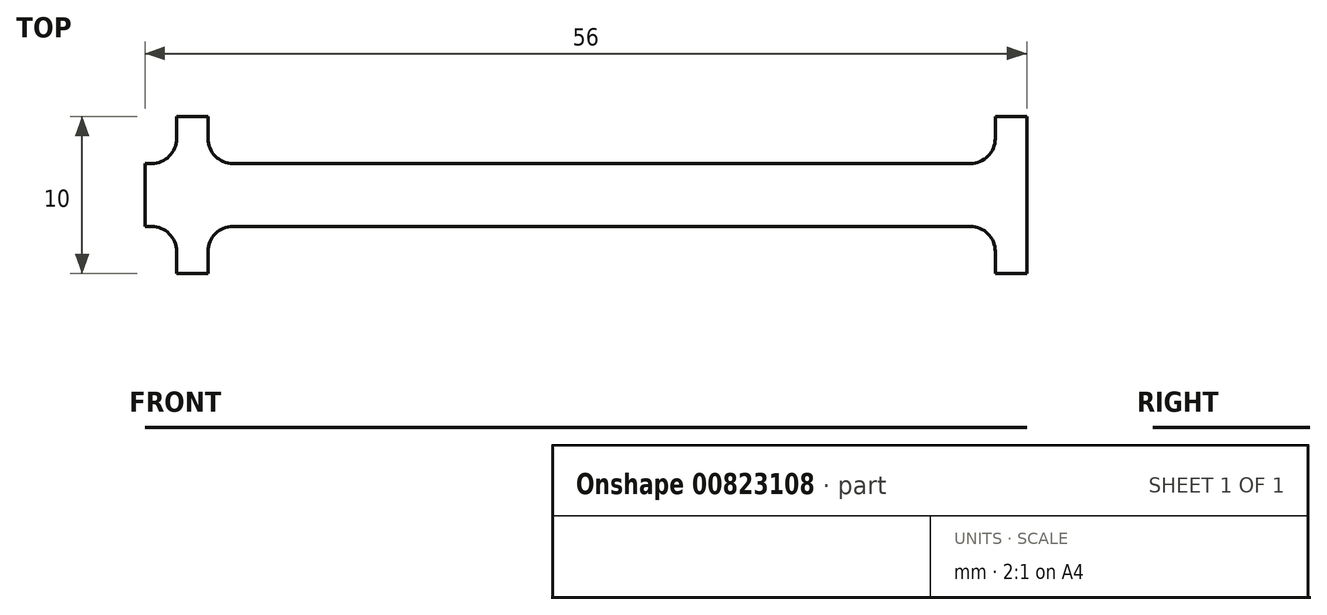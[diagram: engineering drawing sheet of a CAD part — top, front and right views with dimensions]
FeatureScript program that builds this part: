
annotation { "Feature Type Name" : "Feature", "Feature Type Description" : "" }
export const myFeature = defineFeature(function(context is Context, id is Id, definition is map)
    precondition{}
    {
        {
            var Q0;
            Q0=qCreatedBy(makeId("Top.planeOp"),FACE);
            var sketch = newSketch(context, id + "F0", { "sketchPlane" : qUnion([Q0])});
            skLineSegment(sketch, "E0.bottom", {"start": v(-1.59, 2) * mm, "end": v(-48.41, 2) * mm});
            skLineSegment(sketch, "E0.top", {"start": v(-1.59, -2) * mm, "end": v(-48.41, -2) * mm});
            skLineSegment(sketch, "E1.bottom", {"start": v(0, 5) * mm, "end": v(2, 5) * mm});
            skLineSegment(sketch, "E1.top", {"start": v(0, -5) * mm, "end": v(2, -5) * mm});
            skLineSegment(sketch, "E1.left", {"start": v(0, 5) * mm, "end": v(0, 3.59) * mm});
            skLineSegment(sketch, "E1.right", {"start": v(2, 5) * mm, "end": v(2, -5) * mm});
            skLineSegment(sketch, "E2.trimOffspring", {"start": v(0, -3.59) * mm, "end": v(0, -5) * mm});
            skLineSegment(sketch, "E3.bottom", {"start": v(-50, 5) * mm, "end": v(-52, 5) * mm});
            skLineSegment(sketch, "E3.top", {"start": v(-50, -5) * mm, "end": v(-52, -5) * mm});
            skLineSegment(sketch, "E3.left", {"start": v(-50, 5) * mm, "end": v(-50, 3.59) * mm});
            skLineSegment(sketch, "E3.right", {"start": v(-52, 5) * mm, "end": v(-52, 3.59) * mm});
            skLineSegment(sketch, "E4.trimOffspring", {"start": v(-50, -3.59) * mm, "end": v(-50, -5) * mm});
            skPoint(sketch, "E5.visualSharp", {"position": v(-50, 2) * mm});
            skArc(sketch, "E5.filletArc", {"start": v(-50, 3.59) * mm, "mid": v(-49.54, 2.46) * mm, "end": v(-48.41, 2) * mm});
            skPoint(sketch, "E6.visualSharp", {"position": v(-50, -2) * mm});
            skArc(sketch, "E6.filletArc", {"start": v(-48.41, -2) * mm, "mid": v(-49.54, -2.46) * mm, "end": v(-50, -3.59) * mm});
            skPoint(sketch, "E7.visualSharp", {"position": v(0, -2) * mm});
            skArc(sketch, "E7.filletArc", {"start": v(0, -3.59) * mm, "mid": v(-0.46, -2.46) * mm, "end": v(-1.59, -2) * mm});
            skPoint(sketch, "E8.visualSharp", {"position": v(0, 2) * mm});
            skArc(sketch, "E8.filletArc", {"start": v(-1.59, 2) * mm, "mid": v(-0.46, 2.46) * mm, "end": v(0, 3.59) * mm});
            skLineSegment(sketch, "E9.bottom", {"start": v(-53.59, 2) * mm, "end": v(-54, 2) * mm});
            skLineSegment(sketch, "E9.top", {"start": v(-53.59, -2) * mm, "end": v(-54, -2) * mm});
            skLineSegment(sketch, "E9.right", {"start": v(-54, 2) * mm, "end": v(-54, -2) * mm});
            skLineSegment(sketch, "E10.trimOffspring", {"start": v(-52, -3.59) * mm, "end": v(-52, -5) * mm});
            skPoint(sketch, "E11.visualSharp", {"position": v(-52, 2) * mm});
            skArc(sketch, "E11.filletArc", {"start": v(-53.59, 2) * mm, "mid": v(-52.46, 2.46) * mm, "end": v(-52, 3.59) * mm});
            skPoint(sketch, "E12.visualSharp", {"position": v(-52, -2) * mm});
            skArc(sketch, "E12.filletArc", {"start": v(-52, -3.59) * mm, "mid": v(-52.46, -2.46) * mm, "end": v(-53.59, -2) * mm});
            skSolve(sketch);
        }
        {
            var Q0;
            Q0=makeQuery(id+"F0.imprint","IMPRINT",FACE,{"disambiguationData":[TD([[makeQuery(id+"F0.imprint","IMPRINT",EDGE,{"derivedFrom":sQuery(id+"F0.wireOp",EDGE,"E0.bottom")}),1.0]])]});
            extrude(context, id + "F1", {"entities" : qUnion([Q0]), "depth" : 1 / 812.8 * mm, "offsetDistance" : 25 * mm});
        }
    });
